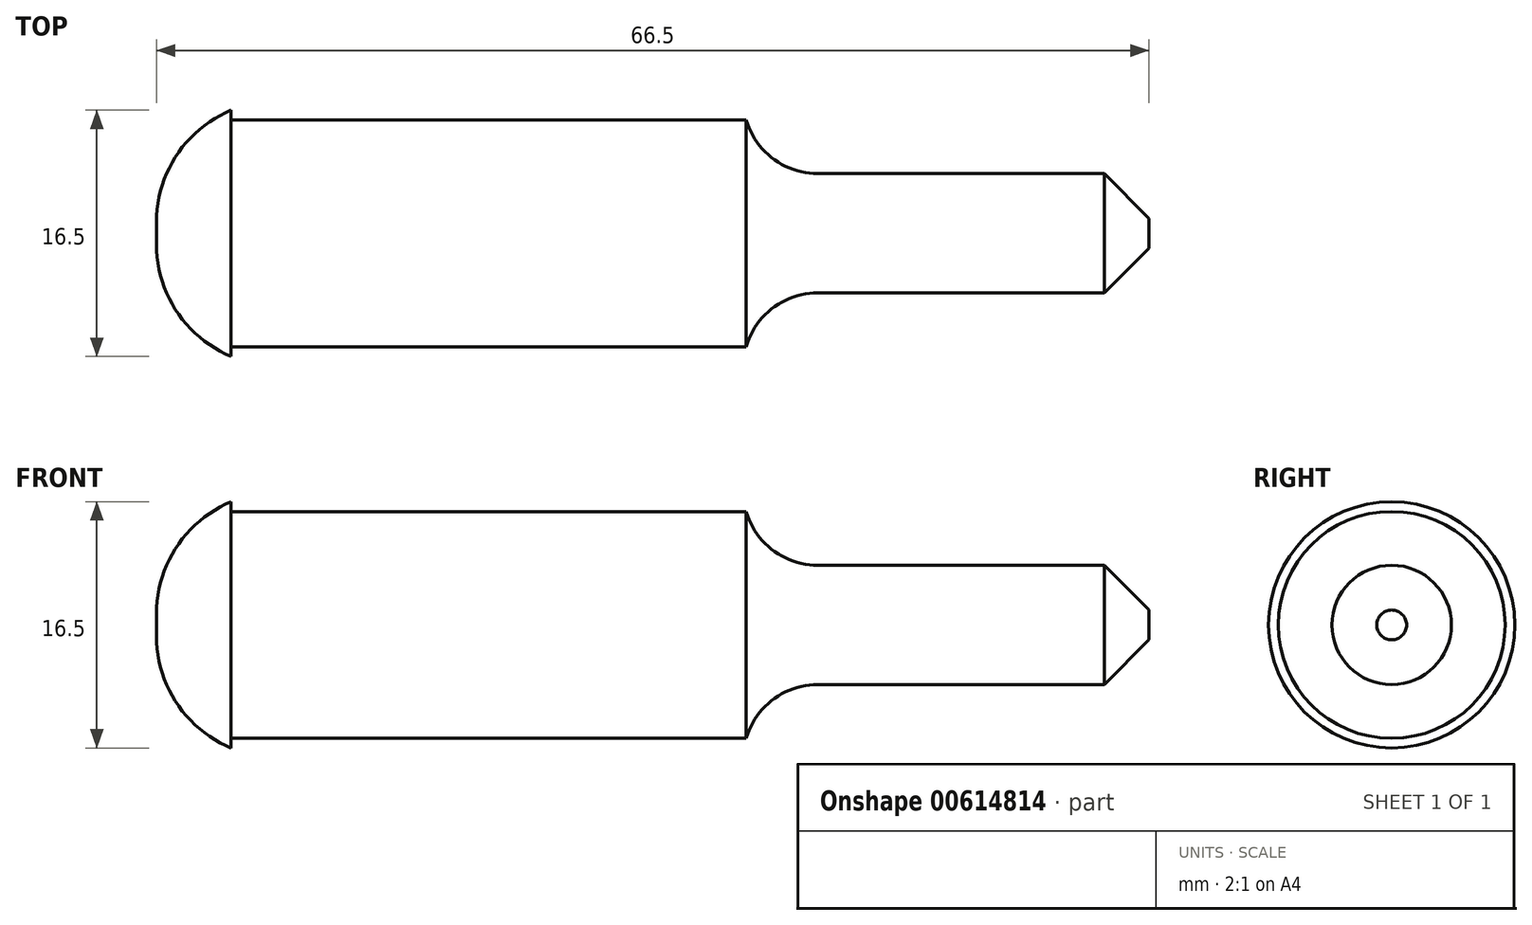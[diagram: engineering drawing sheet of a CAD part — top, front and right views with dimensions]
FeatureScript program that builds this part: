
annotation { "Feature Type Name" : "Feature", "Feature Type Description" : "" }
export const myFeature = defineFeature(function(context is Context, id is Id, definition is map)
    precondition{}
    {
        {
            var Q0;
            Q0=qCreatedBy(makeId("Front.planeOp"),FACE);
            var sketch = newSketch(context, id + "F0", { "sketchPlane" : qUnion([Q0])});
            skLineSegment(sketch, "E0", {"start": v(2, 7.6) * mm, "end": v(36.5, 7.6) * mm});
            skLineSegment(sketch, "E1", {"start": v(36.5, 7.6) * mm, "end": v(36.5, 4) * mm});
            skLineSegment(sketch, "E2", {"start": v(36.5, 4) * mm, "end": v(63.5, 4) * mm});
            skLineSegment(sketch, "E3", {"start": v(63.5, 4) * mm, "end": v(63.5, 0) * mm});
            skLineSegment(sketch, "E4", {"start": v(63.5, 0) * mm, "end": v(0, 0) * mm});
            skLineSegment(sketch, "E5", {"start": v(0, 0) * mm, "end": v(0, 7.6) * mm});
            skLineSegment(sketch, "E6", {"start": v(2, 8.25) * mm, "end": v(-3, 8.25) * mm});
            skLineSegment(sketch, "E7", {"start": v(-3, 8.25) * mm, "end": v(-3, 0) * mm});
            skLineSegment(sketch, "E8", {"start": v(-3, 0) * mm, "end": v(0, 0) * mm});
            skLineSegment(sketch, "E9", {"start": v(2, 8.25) * mm, "end": v(2, 7.6) * mm});
            skSolve(sketch);
        }
        {
            var Q0;
            Q0=makeQuery(id+"F0.imprint","IMPRINT",FACE,{"disambiguationData":[TD([[makeQuery(id+"F0.imprint","IMPRINT",EDGE,{"derivedFrom":sQuery(id+"F0.wireOp",EDGE,"E0")}),-1.0]])]});
            var Q1;
            Q1=sQuery(id+"F0.wireOp",EDGE,"E4");
            revolve(context, id + "F1", {"entities" : qUnion([Q0]), "axis" : qUnion([Q1]), "revolveType" : RevolveType.FULL});
        }
        {
            var Q0;
            Q0=makeQuery(id+"F1.opRevolve","SWEPT_EDGE",EDGE,{"disambiguationData":[OSD([sQuery(id+"F0.wireOp",EDGE,"E1"),sQuery(id+"F0.wireOp",EDGE,"E2")])]});
            fillet(context, id + "F2", {"entities" : qUnion([Q0]), "radius" : 5 * mm, "tangentPropagation" : true, "allowEdgeOverflow" : false});
        }
        {
            var Q0;
            Q0=makeQuery(id+"F1.opRevolve","SWEPT_EDGE",EDGE,{"disambiguationData":[OSD([sQuery(id+"F0.wireOp",EDGE,"E2"),sQuery(id+"F0.wireOp",EDGE,"E3")])]});
            chamfer(context, id + "F3", {"entities" : qUnion([Q0]), "width" : 3 * mm, "tangentPropagation" : true});
        }
        {
            var Q0;
            Q0=makeQuery(id+"F1.opRevolve","SWEPT_EDGE",EDGE,{"disambiguationData":[OSD([sQuery(id+"F0.wireOp",EDGE,"E6"),sQuery(id+"F0.wireOp",EDGE,"E7")])]});
            fillet(context, id + "F4", {"entities" : qUnion([Q0]), "radius" : 8.1 * mm, "tangentPropagation" : true, "allowEdgeOverflow" : false});
        }
    });
